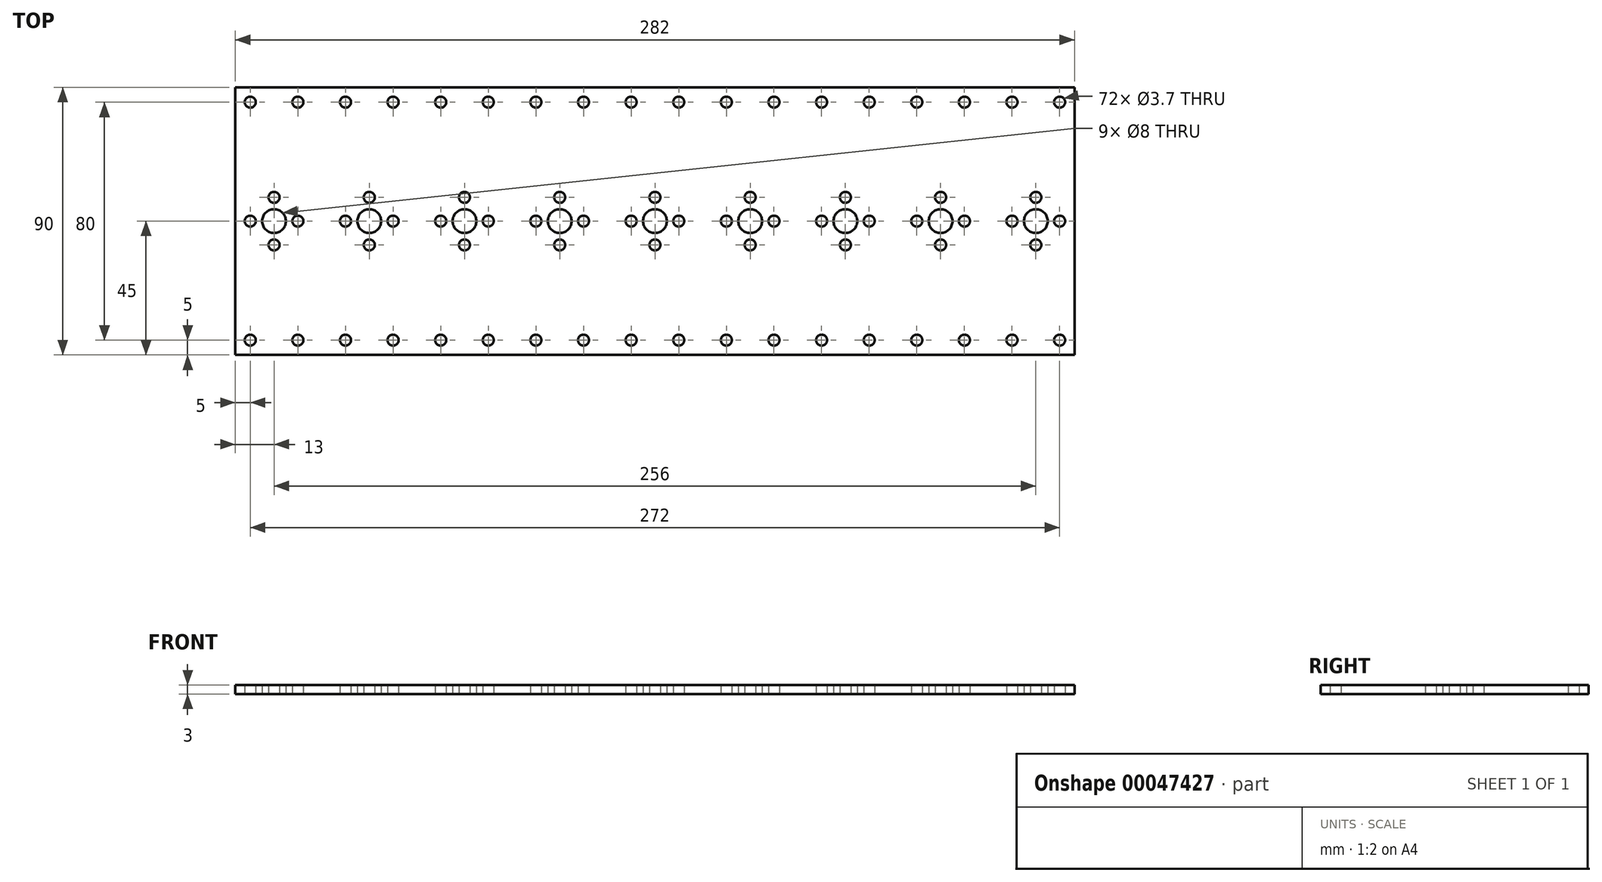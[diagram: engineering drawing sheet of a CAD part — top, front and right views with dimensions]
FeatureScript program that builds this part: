
annotation { "Feature Type Name" : "Feature", "Feature Type Description" : "" }
export const myFeature = defineFeature(function(context is Context, id is Id, definition is map)
    precondition{}
    {
        {
            var Q0;
            Q0=qCreatedBy(makeId("Top.planeOp"),FACE);
            var sketch = newSketch(context, id + "F0", { "sketchPlane" : qUnion([Q0])});
            skLineSegment(sketch, "E0.rect.bottom", {"start": v(-141, -45) * mm, "end": v(141, -45) * mm});
            skLineSegment(sketch, "E0.rect.top", {"start": v(-141, 45) * mm, "end": v(141, 45) * mm});
            skLineSegment(sketch, "E0.rect.left", {"start": v(-141, -45) * mm, "end": v(-141, 45) * mm});
            skLineSegment(sketch, "E0.rect.right", {"start": v(141, -45) * mm, "end": v(141, 45) * mm});
            skPoint(sketch, "E0.rect.middle", {"position": v(0, 0) * mm});
            skCircle(sketch, "E1", {"center": v(0, 0) * mm, "radius": 4 * mm});
            skCircle(sketch, "E2", {"center": v(0, -8) * mm, "radius": 1.85 * mm});
            skCircle(sketch, "E3.1.0", {"center": v(8, 0) * mm, "radius": 1.85 * mm});
            skCircle(sketch, "E3.2.0", {"center": v(0, 8) * mm, "radius": 1.85 * mm});
            skCircle(sketch, "E3.3.0", {"center": v(-8, 0) * mm, "radius": 1.85 * mm});
            skPoint(sketch, "E4.1.0.0", {"position": v(32, 0) * mm});
            skCircle(sketch, "E4.1.0.1", {"center": v(32, 0) * mm, "radius": 4 * mm});
            skCircle(sketch, "E4.1.0.2", {"center": v(40, 0) * mm, "radius": 1.85 * mm});
            skCircle(sketch, "E4.1.0.3", {"center": v(32, 8) * mm, "radius": 1.85 * mm});
            skPoint(sketch, "E4.1.0.4", {"position": v(32, 0) * mm});
            skCircle(sketch, "E4.1.0.5", {"center": v(24, 0) * mm, "radius": 1.85 * mm});
            skCircle(sketch, "E4.1.0.6", {"center": v(32, -8) * mm, "radius": 1.85 * mm});
            skPoint(sketch, "E4.2.0.0", {"position": v(64, 0) * mm});
            skCircle(sketch, "E4.2.0.1", {"center": v(64, 0) * mm, "radius": 4 * mm});
            skCircle(sketch, "E4.2.0.2", {"center": v(72, 0) * mm, "radius": 1.85 * mm});
            skCircle(sketch, "E4.2.0.3", {"center": v(64, 8) * mm, "radius": 1.85 * mm});
            skPoint(sketch, "E4.2.0.4", {"position": v(64, 0) * mm});
            skCircle(sketch, "E4.2.0.5", {"center": v(56, 0) * mm, "radius": 1.85 * mm});
            skCircle(sketch, "E4.2.0.6", {"center": v(64, -8) * mm, "radius": 1.85 * mm});
            skPoint(sketch, "E4.3.0.0", {"position": v(96, 0) * mm});
            skCircle(sketch, "E4.3.0.1", {"center": v(96, 0) * mm, "radius": 4 * mm});
            skCircle(sketch, "E4.3.0.2", {"center": v(104, 0) * mm, "radius": 1.85 * mm});
            skCircle(sketch, "E4.3.0.3", {"center": v(96, 8) * mm, "radius": 1.85 * mm});
            skPoint(sketch, "E4.3.0.4", {"position": v(96, 0) * mm});
            skCircle(sketch, "E4.3.0.5", {"center": v(88, 0) * mm, "radius": 1.85 * mm});
            skCircle(sketch, "E4.3.0.6", {"center": v(96, -8) * mm, "radius": 1.85 * mm});
            skPoint(sketch, "E4.4.0.0", {"position": v(128, 0) * mm});
            skCircle(sketch, "E4.4.0.1", {"center": v(128, 0) * mm, "radius": 4 * mm});
            skCircle(sketch, "E4.4.0.2", {"center": v(136, 0) * mm, "radius": 1.85 * mm});
            skCircle(sketch, "E4.4.0.3", {"center": v(128, 8) * mm, "radius": 1.85 * mm});
            skPoint(sketch, "E4.4.0.4", {"position": v(128, 0) * mm});
            skCircle(sketch, "E4.4.0.5", {"center": v(120, 0) * mm, "radius": 1.85 * mm});
            skCircle(sketch, "E4.4.0.6", {"center": v(128, -8) * mm, "radius": 1.85 * mm});
            skLineSegment(sketch, "E4.direction1", {"start": v(0, 0) * mm, "end": v(32, 0) * mm, "construction": true});
            skCircle(sketch, "E5.1.0.0", {"center": v(-32, 0) * mm, "radius": 4 * mm});
            skCircle(sketch, "E5.1.0.1", {"center": v(-32, -8) * mm, "radius": 1.85 * mm});
            skCircle(sketch, "E5.1.0.2", {"center": v(-24, 0) * mm, "radius": 1.85 * mm});
            skCircle(sketch, "E5.1.0.3", {"center": v(-32, 8) * mm, "radius": 1.85 * mm});
            skCircle(sketch, "E5.1.0.4", {"center": v(-40, 0) * mm, "radius": 1.85 * mm});
            skPoint(sketch, "E5.1.0.5", {"position": v(-32, 0) * mm});
            skPoint(sketch, "E5.1.0.6", {"position": v(-32, 0) * mm});
            skCircle(sketch, "E5.2.0.0", {"center": v(-64, 0) * mm, "radius": 4 * mm});
            skCircle(sketch, "E5.2.0.1", {"center": v(-64, -8) * mm, "radius": 1.85 * mm});
            skCircle(sketch, "E5.2.0.2", {"center": v(-56, 0) * mm, "radius": 1.85 * mm});
            skCircle(sketch, "E5.2.0.3", {"center": v(-64, 8) * mm, "radius": 1.85 * mm});
            skCircle(sketch, "E5.2.0.4", {"center": v(-72, 0) * mm, "radius": 1.85 * mm});
            skPoint(sketch, "E5.2.0.5", {"position": v(-64, 0) * mm});
            skPoint(sketch, "E5.2.0.6", {"position": v(-64, 0) * mm});
            skCircle(sketch, "E5.3.0.0", {"center": v(-96, 0) * mm, "radius": 4 * mm});
            skCircle(sketch, "E5.3.0.1", {"center": v(-96, -8) * mm, "radius": 1.85 * mm});
            skCircle(sketch, "E5.3.0.2", {"center": v(-88, 0) * mm, "radius": 1.85 * mm});
            skCircle(sketch, "E5.3.0.3", {"center": v(-96, 8) * mm, "radius": 1.85 * mm});
            skCircle(sketch, "E5.3.0.4", {"center": v(-104, 0) * mm, "radius": 1.85 * mm});
            skPoint(sketch, "E5.3.0.5", {"position": v(-96, 0) * mm});
            skPoint(sketch, "E5.3.0.6", {"position": v(-96, 0) * mm});
            skCircle(sketch, "E5.4.0.0", {"center": v(-128, 0) * mm, "radius": 4 * mm});
            skCircle(sketch, "E5.4.0.1", {"center": v(-128, -8) * mm, "radius": 1.85 * mm});
            skCircle(sketch, "E5.4.0.2", {"center": v(-120, 0) * mm, "radius": 1.85 * mm});
            skCircle(sketch, "E5.4.0.3", {"center": v(-128, 8) * mm, "radius": 1.85 * mm});
            skCircle(sketch, "E5.4.0.4", {"center": v(-136, 0) * mm, "radius": 1.85 * mm});
            skPoint(sketch, "E5.4.0.5", {"position": v(-128, 0) * mm});
            skPoint(sketch, "E5.4.0.6", {"position": v(-128, 0) * mm});
            skLineSegment(sketch, "E5.direction1", {"start": v(0, 0) * mm, "end": v(-32, 0) * mm, "construction": true});
            skLineSegment(sketch, "E6", {"start": v(-136, 0) * mm, "end": v(-136, -40) * mm, "construction": true});
            skCircle(sketch, "E7", {"center": v(-136, -40) * mm, "radius": 1.85 * mm});
            skCircle(sketch, "E8.1.0.0", {"center": v(-120, -40) * mm, "radius": 1.85 * mm});
            skCircle(sketch, "E8.2.0.0", {"center": v(-104, -40) * mm, "radius": 1.85 * mm});
            skCircle(sketch, "E8.3.0.0", {"center": v(-88, -40) * mm, "radius": 1.85 * mm});
            skCircle(sketch, "E8.4.0.0", {"center": v(-72, -40) * mm, "radius": 1.85 * mm});
            skCircle(sketch, "E8.5.0.0", {"center": v(-56, -40) * mm, "radius": 1.85 * mm});
            skCircle(sketch, "E8.6.0.0", {"center": v(-40, -40) * mm, "radius": 1.85 * mm});
            skCircle(sketch, "E8.7.0.0", {"center": v(-24, -40) * mm, "radius": 1.85 * mm});
            skCircle(sketch, "E8.8.0.0", {"center": v(-8, -40) * mm, "radius": 1.85 * mm});
            skCircle(sketch, "E8.9.0.0", {"center": v(8, -40) * mm, "radius": 1.85 * mm});
            skCircle(sketch, "E8.10.0.0", {"center": v(24, -40) * mm, "radius": 1.85 * mm});
            skCircle(sketch, "E8.11.0.0", {"center": v(40, -40) * mm, "radius": 1.85 * mm});
            skCircle(sketch, "E8.12.0.0", {"center": v(56, -40) * mm, "radius": 1.85 * mm});
            skCircle(sketch, "E8.13.0.0", {"center": v(72, -40) * mm, "radius": 1.85 * mm});
            skCircle(sketch, "E8.14.0.0", {"center": v(88, -40) * mm, "radius": 1.85 * mm});
            skCircle(sketch, "E8.15.0.0", {"center": v(104, -40) * mm, "radius": 1.85 * mm});
            skCircle(sketch, "E8.16.0.0", {"center": v(120, -40) * mm, "radius": 1.85 * mm});
            skCircle(sketch, "E8.17.0.0", {"center": v(136, -40) * mm, "radius": 1.85 * mm});
            skLineSegment(sketch, "E8.direction1", {"start": v(-136, -40) * mm, "end": v(-120, -40) * mm, "construction": true});
            skLineSegment(sketch, "E9", {"start": v(-136, 0) * mm, "end": v(-136, 40) * mm, "construction": true});
            skCircle(sketch, "E10", {"center": v(-136, 40) * mm, "radius": 1.85 * mm});
            skCircle(sketch, "E11.1.0.0", {"center": v(-120, 40) * mm, "radius": 1.85 * mm});
            skCircle(sketch, "E11.2.0.0", {"center": v(-104, 40) * mm, "radius": 1.85 * mm});
            skCircle(sketch, "E11.3.0.0", {"center": v(-88, 40) * mm, "radius": 1.85 * mm});
            skCircle(sketch, "E11.4.0.0", {"center": v(-72, 40) * mm, "radius": 1.85 * mm});
            skCircle(sketch, "E11.5.0.0", {"center": v(-56, 40) * mm, "radius": 1.85 * mm});
            skCircle(sketch, "E11.6.0.0", {"center": v(-40, 40) * mm, "radius": 1.85 * mm});
            skCircle(sketch, "E11.7.0.0", {"center": v(-24, 40) * mm, "radius": 1.85 * mm});
            skCircle(sketch, "E11.8.0.0", {"center": v(-8, 40) * mm, "radius": 1.85 * mm});
            skCircle(sketch, "E11.9.0.0", {"center": v(8, 40) * mm, "radius": 1.85 * mm});
            skCircle(sketch, "E11.10.0.0", {"center": v(24, 40) * mm, "radius": 1.85 * mm});
            skCircle(sketch, "E11.11.0.0", {"center": v(40, 40) * mm, "radius": 1.85 * mm});
            skCircle(sketch, "E11.12.0.0", {"center": v(56, 40) * mm, "radius": 1.85 * mm});
            skCircle(sketch, "E11.13.0.0", {"center": v(72, 40) * mm, "radius": 1.85 * mm});
            skCircle(sketch, "E11.14.0.0", {"center": v(88, 40) * mm, "radius": 1.85 * mm});
            skCircle(sketch, "E11.15.0.0", {"center": v(104, 40) * mm, "radius": 1.85 * mm});
            skCircle(sketch, "E11.16.0.0", {"center": v(120, 40) * mm, "radius": 1.85 * mm});
            skCircle(sketch, "E11.17.0.0", {"center": v(136, 40) * mm, "radius": 1.85 * mm});
            skLineSegment(sketch, "E11.direction1", {"start": v(-136, 40) * mm, "end": v(-120, 40) * mm, "construction": true});
            skSolve(sketch);
        }
        {
            var Q0;
            Q0=makeQuery(id+"F0.imprint","IMPRINT",FACE,{"disambiguationData":[TD([[makeQuery(id+"F0.imprint","IMPRINT",EDGE,{"derivedFrom":sQuery(id+"F0.wireOp",EDGE,"E0.rect.bottom")}),1.0]])]});
            extrude(context, id + "F1", {"entities" : qUnion([Q0]), "depth" : 3 * mm});
        }
    });
